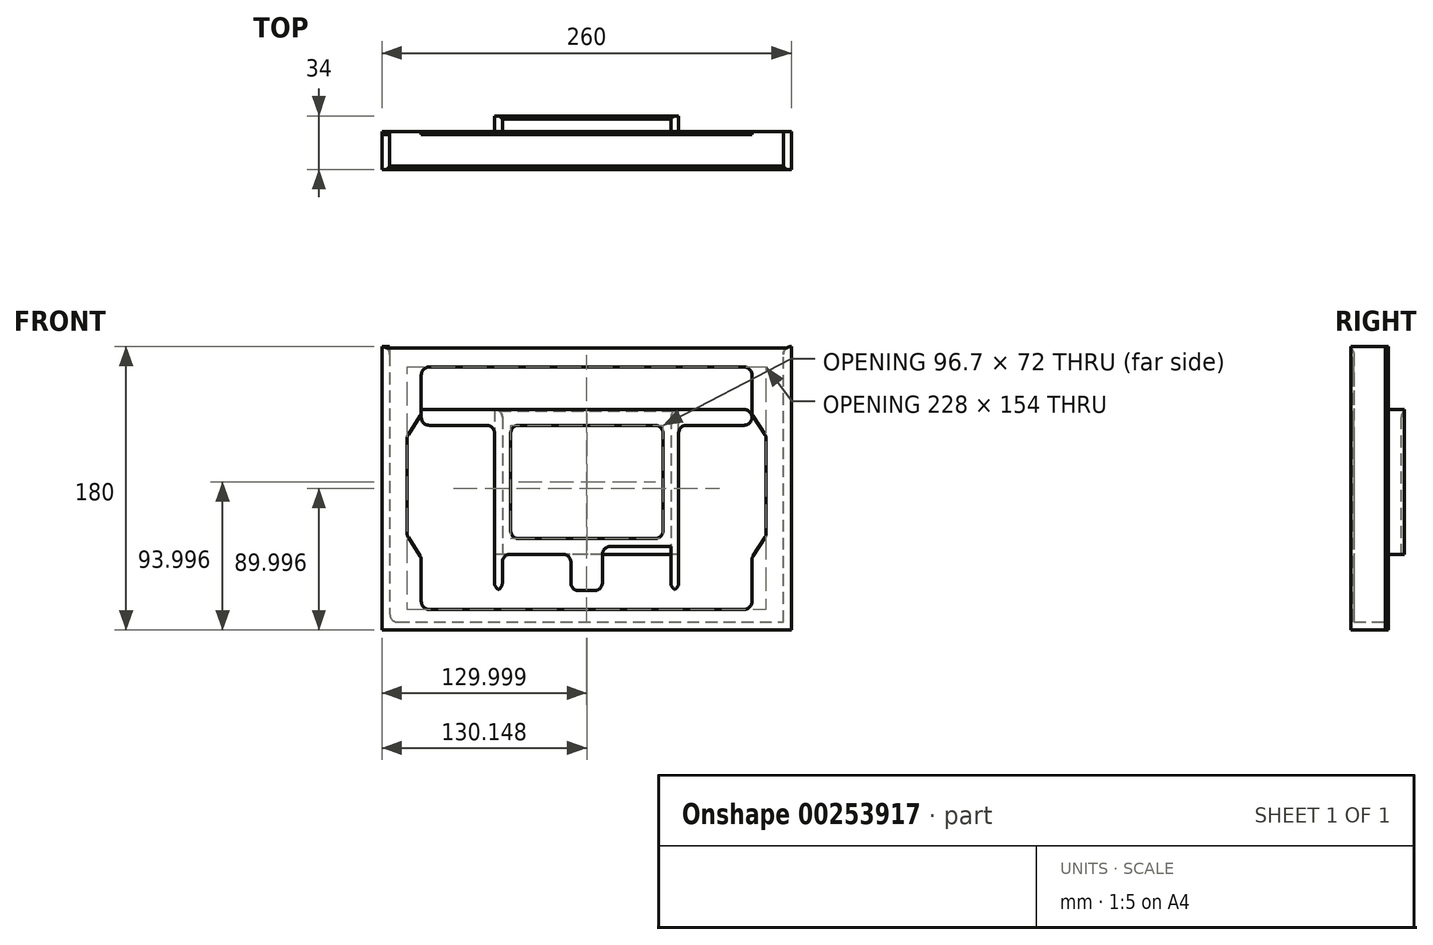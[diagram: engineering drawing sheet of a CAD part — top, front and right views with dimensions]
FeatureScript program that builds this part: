
annotation { "Feature Type Name" : "Feature", "Feature Type Description" : "" }
export const myFeature = defineFeature(function(context is Context, id is Id, definition is map)
    precondition{}
    {
        {
            var Q0;
            Q0=qCreatedBy(makeId("Front.planeOp"),FACE);
            var sketch = newSketch(context, id + "F0", { "sketchPlane" : qUnion([Q0])});
            skLineSegment(sketch, "E0", {"start": v(-163.92, 87.23) * mm, "end": v(-163.92, -87.77) * mm});
            skLineSegment(sketch, "E1", {"start": v(-163.92, -87.77) * mm, "end": v(86.08, -87.77) * mm});
            skLineSegment(sketch, "E2", {"start": v(86.08, -87.77) * mm, "end": v(86.08, 87.23) * mm});
            skLineSegment(sketch, "E3", {"start": v(86.08, 87.23) * mm, "end": v(91.08, 87.23) * mm});
            skLineSegment(sketch, "E4", {"start": v(91.08, 87.23) * mm, "end": v(91.08, -92.77) * mm});
            skLineSegment(sketch, "E5", {"start": v(91.08, -92.77) * mm, "end": v(-168.92, -92.77) * mm});
            skLineSegment(sketch, "E6", {"start": v(-168.92, -92.77) * mm, "end": v(-168.92, 87.23) * mm});
            skLineSegment(sketch, "E7", {"start": v(-168.92, 87.23) * mm, "end": v(-163.92, 87.23) * mm});
            skSolve(sketch);
        }
        {
            var Q0;
            Q0 = qSketchRegion(id + "F0", true);
            extrude(context, id + "F1", {"entities" : qUnion([Q0]), "depth" : 20 * mm});
        }
        {
            var Q0;
            Q0=makeQuery(id+"F1.opExtrude","CAP_FACE",FACE,{"disambiguationData":[OSD([sQuery(id+"F0.wireOp",EDGE,"E0"),sQuery(id+"F0.wireOp",EDGE,"E1"),sQuery(id+"F0.wireOp",EDGE,"E2"),sQuery(id+"F0.wireOp",EDGE,"E3"),sQuery(id+"F0.wireOp",EDGE,"E4"),sQuery(id+"F0.wireOp",EDGE,"E5"),sQuery(id+"F0.wireOp",EDGE,"E6"),sQuery(id+"F0.wireOp",EDGE,"E7")])],"isStart":false});
            var sketch = newSketch(context, id + "F2", { "sketchPlane" : qUnion([Q0])});
            skLineSegment(sketch, "E8", {"start": v(91.08, 87.23) * mm, "end": v(91.08, -92.77) * mm});
            skLineSegment(sketch, "E9", {"start": v(91.08, -92.77) * mm, "end": v(-168.92, -92.77) * mm});
            skLineSegment(sketch, "E10", {"start": v(-168.92, -92.77) * mm, "end": v(-168.92, 87.23) * mm});
            skLineSegment(sketch, "E11", {"start": v(-168.92, 87.23) * mm, "end": v(91.08, 87.23) * mm});
            skLineSegment(sketch, "E12", {"start": v(-143.92, 74.23) * mm, "end": v(-143.92, 44.23) * mm});
            skLineSegment(sketch, "E13", {"start": v(-152.92, 30.23) * mm, "end": v(-152.92, -32.96) * mm});
            skLineSegment(sketch, "E14", {"start": v(-143.92, -46.96) * mm, "end": v(-143.92, -79.77) * mm});
            skLineSegment(sketch, "E15", {"start": v(-143.92, 44.23) * mm, "end": v(-152.92, 30.23) * mm});
            skLineSegment(sketch, "E16", {"start": v(-143.92, -46.96) * mm, "end": v(-152.92, -32.96) * mm});
            skLineSegment(sketch, "E17", {"start": v(75.08, 30.23) * mm, "end": v(75.08, -32.96) * mm});
            skLineSegment(sketch, "E18", {"start": v(-143.92, 74.23) * mm, "end": v(66.08, 74.23) * mm});
            skLineSegment(sketch, "E19", {"start": v(66.08, -79.77) * mm, "end": v(-143.92, -79.77) * mm});
            skLineSegment(sketch, "E20", {"start": v(75.08, 30.23) * mm, "end": v(66.08, 44.23) * mm});
            skLineSegment(sketch, "E21", {"start": v(75.08, -32.96) * mm, "end": v(66.08, -46.96) * mm});
            skLineSegment(sketch, "E22", {"start": v(66.08, 44.23) * mm, "end": v(66.08, 74.23) * mm});
            skLineSegment(sketch, "E23", {"start": v(66.08, -46.96) * mm, "end": v(66.08, -79.77) * mm});
            skSolve(sketch);
        }
        {
            var Q0;
            Q0 = qSketchRegion(id + "F2", true);
            extrude(context, id + "F3", {"entities" : qUnion([Q0]), "operationType" : NewBodyOperationType.ADD, "depth" : 2 * mm});
        }
        {
            var Q0;
            Q0=makeQuery(id+"F0.imprint","IMPRINT",FACE,{"disambiguationData":[TD([[makeQuery(id+"F0.imprint","IMPRINT",EDGE,{"derivedFrom":sQuery(id+"F0.wireOp",EDGE,"E0")}),-1.0]])]});
            var sketch = newSketch(context, id + "F4", { "sketchPlane" : qUnion([Q0])});
            skLineSegment(sketch, "E24", {"start": v(91.08, 87.23) * mm, "end": v(91.08, -92.77) * mm});
            skLineSegment(sketch, "E25", {"start": v(91.08, -92.77) * mm, "end": v(-168.92, -92.77) * mm});
            skLineSegment(sketch, "E26", {"start": v(-168.92, -92.77) * mm, "end": v(-168.92, 87.23) * mm});
            skLineSegment(sketch, "E27", {"start": v(-168.92, 87.23) * mm, "end": v(-143.92, 87.23) * mm});
            skLineSegment(sketch, "E28", {"start": v(-143.92, 87.23) * mm, "end": v(-143.92, -87.77) * mm});
            skLineSegment(sketch, "E29", {"start": v(66.08, -87.77) * mm, "end": v(66.08, 87.23) * mm});
            skLineSegment(sketch, "E30", {"start": v(66.08, 87.23) * mm, "end": v(91.08, 87.23) * mm});
            skLineSegment(sketch, "E31", {"start": v(66.08, 87.23) * mm, "end": v(66.08, 47.23) * mm});
            skLineSegment(sketch, "E32", {"start": v(66.08, 47.23) * mm, "end": v(-143.92, 47.23) * mm});
            skLineSegment(sketch, "E33", {"start": v(-143.92, 47.23) * mm, "end": v(-143.92, 37.23) * mm});
            skLineSegment(sketch, "E34", {"start": v(-143.92, 37.23) * mm, "end": v(66.08, 37.23) * mm});
            skLineSegment(sketch, "E35", {"start": v(66.08, -87.77) * mm, "end": v(66.08, -67.77) * mm});
            skLineSegment(sketch, "E36", {"start": v(66.08, -67.77) * mm, "end": v(-143.92, -67.77) * mm});
            skLineSegment(sketch, "E37.bottom", {"start": v(66.08, 37.23) * mm, "end": v(14.58, 37.23) * mm});
            skLineSegment(sketch, "E37.top", {"start": v(66.08, 37.23) * mm, "end": v(14.58, 37.23) * mm});
            skLineSegment(sketch, "E37.left", {"start": v(66.08, 37.23) * mm, "end": v(66.08, 37.23) * mm});
            skLineSegment(sketch, "E37.right", {"start": v(14.58, 37.23) * mm, "end": v(14.58, 37.23) * mm});
            skLineSegment(sketch, "E38.bottom", {"start": v(-143.92, 37.23) * mm, "end": v(-92.42, 37.23) * mm});
            skLineSegment(sketch, "E38.top", {"start": v(-143.92, 37.23) * mm, "end": v(-92.42, 37.23) * mm});
            skLineSegment(sketch, "E38.left", {"start": v(-143.92, 37.23) * mm, "end": v(-143.92, 37.23) * mm});
            skLineSegment(sketch, "E38.right", {"start": v(-92.42, 37.23) * mm, "end": v(-92.42, 37.23) * mm});
            skLineSegment(sketch, "E39", {"start": v(14.58, 37.23) * mm, "end": v(14.58, -39.77) * mm});
            skLineSegment(sketch, "E40", {"start": v(14.58, -39.77) * mm, "end": v(-92.42, -39.77) * mm});
            skLineSegment(sketch, "E41", {"start": v(-92.42, -39.77) * mm, "end": v(-92.42, 37.23) * mm});
            skLineSegment(sketch, "E42", {"start": v(14.58, 37.23) * mm, "end": v(19.58, 37.23) * mm});
            skLineSegment(sketch, "E43", {"start": v(19.58, 37.23) * mm, "end": v(19.58, -58.16) * mm});
            skLineSegment(sketch, "E44", {"start": v(14.58, -39.77) * mm, "end": v(14.58, -67.77) * mm});
            skLineSegment(sketch, "E45", {"start": v(19.58, -58.16) * mm, "end": v(19.58, -67.77) * mm});
            skLineSegment(sketch, "E46", {"start": v(-92.42, 37.23) * mm, "end": v(-97.42, 37.23) * mm});
            skLineSegment(sketch, "E47", {"start": v(-97.42, 37.23) * mm, "end": v(-97.42, -67.77) * mm});
            skLineSegment(sketch, "E48", {"start": v(-92.42, -39.77) * mm, "end": v(-92.42, -67.77) * mm});
            skLineSegment(sketch, "E49", {"start": v(14.58, -67.77) * mm, "end": v(-28.92, -67.77) * mm});
            skLineSegment(sketch, "E50", {"start": v(-28.92, -67.77) * mm, "end": v(-28.92, -39.77) * mm});
            skLineSegment(sketch, "E51", {"start": v(-92.42, -67.77) * mm, "end": v(-48.92, -67.77) * mm});
            skLineSegment(sketch, "E52", {"start": v(-48.92, -67.77) * mm, "end": v(-48.92, -39.77) * mm});
            skLineSegment(sketch, "E53", {"start": v(14.58, -39.77) * mm, "end": v(14.58, -44.77) * mm});
            skLineSegment(sketch, "E54", {"start": v(14.58, -44.77) * mm, "end": v(-92.42, -44.77) * mm});
            skLineSegment(sketch, "E55", {"start": v(91.08, 87.23) * mm, "end": v(86.08, 87.23) * mm});
            skLineSegment(sketch, "E56", {"start": v(86.08, 87.23) * mm, "end": v(86.08, 47.23) * mm});
            skLineSegment(sketch, "E57", {"start": v(86.08, 47.23) * mm, "end": v(66.08, 47.23) * mm});
            skLineSegment(sketch, "E58", {"start": v(-168.92, 87.23) * mm, "end": v(-163.92, 87.23) * mm});
            skLineSegment(sketch, "E59", {"start": v(-163.92, 87.23) * mm, "end": v(-163.92, 47.23) * mm});
            skLineSegment(sketch, "E60", {"start": v(-163.92, 47.23) * mm, "end": v(-143.92, 47.23) * mm});
            skLineSegment(sketch, "E61", {"start": v(-92.42, 37.23) * mm, "end": v(-87.12, 37.23) * mm});
            skLineSegment(sketch, "E62", {"start": v(-87.12, 37.23) * mm, "end": v(-87.12, -34.77) * mm});
            skLineSegment(sketch, "E63", {"start": v(14.58, 37.23) * mm, "end": v(9.58, 37.23) * mm});
            skLineSegment(sketch, "E64", {"start": v(9.58, 37.23) * mm, "end": v(9.58, -34.77) * mm});
            skLineSegment(sketch, "E65", {"start": v(9.58, -34.77) * mm, "end": v(-87.12, -34.77) * mm});
            skSolve(sketch);
        }
        {
            var Q0;
            {var subQ0=sQuery(id+"F4.wireOp",EDGE,"E32");Q0=makeQuery(id+"F4.imprint","IMPRINT",FACE,{"disambiguationData":[TD([[makeQuery(id+"F4.imprint","IMPRINT",EDGE,{"derivedFrom":subQ0}),1.0]])]});}
            var Q1;
            Q1=makeQuery(id+"F4.imprint","IMPRINT",FACE,{"disambiguationData":[TD([[makeQuery(id+"F4.imprint","IMPRINT",EDGE,{"derivedFrom":makeQuery(id+"F0.imprint","IMPRINT",EDGE,{"derivedFrom":sQuery(id+"F0.wireOp",EDGE,"E0")})}),-1.0]])]});
            var Q2;
            {var subQ13=sQuery(id+"F4.wireOp",EDGE,"E26");Q2=makeQuery(id+"F4.imprint","IMPRINT",FACE,{"disambiguationData":[TD([[makeQuery(id+"F4.imprint","IMPRINT",EDGE,{"derivedFrom":subQ13}),-1.0]])]});}
            var Q3;
            Q3=makeQuery(id+"F4.imprint","IMPRINT",FACE,{"disambiguationData":[TD([[makeQuery(id+"F4.imprint","IMPRINT",EDGE,{"derivedFrom":sQuery(id+"F4.wireOp",EDGE,"E39")}),1.0]])]});
            var Q4;
            {var subQ0=sQuery(id+"F4.wireOp",EDGE,"E53");Q4=makeQuery(id+"F4.imprint","IMPRINT",FACE,{"disambiguationData":[TD([[makeQuery(id+"F4.imprint","IMPRINT",EDGE,{"derivedFrom":subQ0}),-1.0]])]});}
            var Q5;
            {var subQ0=sQuery(id+"F4.wireOp",EDGE,"E50");var subQ5=sQuery(id+"F4.wireOp",EDGE,"E54");var subQ6=makeQuery(id+"F4.imprint","INTERSECT",VERTEX,{"derivedFrom":[subQ0,subQ5]});Q5=makeQuery(id+"F4.imprint","IMPRINT",FACE,{"disambiguationData":[TD([[makeQuery(id+"F4.imprint","IMPRINT",EDGE,{"disambiguationData":[TD([[subQ6,-1.0]])],"derivedFrom":subQ5}),1.0]])]});}
            var Q6;
            {var subQ0=sQuery(id+"F4.wireOp",EDGE,"E50");var subQ1=sQuery(id+"F4.wireOp",EDGE,"E40");var subQ2=makeQuery(id+"F4.imprint","INTERSECT",VERTEX,{"derivedFrom":[subQ1,subQ0]});Q6=makeQuery(id+"F4.imprint","IMPRINT",FACE,{"disambiguationData":[TD([[makeQuery(id+"F4.imprint","IMPRINT",EDGE,{"disambiguationData":[TD([[subQ2,-1.0]])],"derivedFrom":subQ1}),1.0]])]});}
            var Q7;
            {var subQ1=sQuery(id+"F4.wireOp",EDGE,"E40");var subQ3=sQuery(id+"F4.wireOp",EDGE,"E52");var subQ4=makeQuery(id+"F4.imprint","INTERSECT",VERTEX,{"derivedFrom":[subQ1,subQ3]});Q7=makeQuery(id+"F4.imprint","IMPRINT",FACE,{"disambiguationData":[TD([[makeQuery(id+"F4.imprint","IMPRINT",EDGE,{"disambiguationData":[TD([[subQ4,1.0]])],"derivedFrom":subQ3}),1.0]])]});}
            var Q8;
            {var subQ5=sQuery(id+"F4.wireOp",EDGE,"E41");Q8=makeQuery(id+"F4.imprint","IMPRINT",FACE,{"disambiguationData":[TD([[makeQuery(id+"F4.imprint","IMPRINT",EDGE,{"derivedFrom":subQ5}),1.0]])]});}
            var Q9;
            {var subQ14=makeQuery(id+"F0.imprint","IMPRINT",EDGE,{"derivedFrom":sQuery(id+"F0.wireOp",EDGE,"E1")});Q9=makeQuery(id+"F4.imprint","IMPRINT",FACE,{"disambiguationData":[TD([[makeQuery(id+"F4.imprint","IMPRINT",EDGE,{"derivedFrom":subQ14}),-1.0]])]});}
            var Q10;
            {var subQ7=sQuery(id+"F4.wireOp",EDGE,"E33");Q10=makeQuery(id+"F4.imprint","IMPRINT",FACE,{"disambiguationData":[TD([[makeQuery(id+"F4.imprint","IMPRINT",EDGE,{"derivedFrom":subQ7}),-1.0]])]});}
            var Q11;
            {var subQ4=sQuery(id+"F4.wireOp",EDGE,"E39");Q11=makeQuery(id+"F4.imprint","IMPRINT",FACE,{"disambiguationData":[TD([[makeQuery(id+"F4.imprint","IMPRINT",EDGE,{"derivedFrom":subQ4}),-1.0]])]});}
            extrude(context, id + "F5", {"entities" : qUnion([Q0, Q1, Q2, Q3, Q4, Q5, Q6, Q7, Q8, Q9, Q10, Q11]), "operationType" : NewBodyOperationType.ADD, "oppositeDirection" : true, "depth" : 2 * mm});
        }
        {
            var Q0;
            Q0=makeQuery(id+"F5.opExtrude","CAP_FACE",FACE,{"disambiguationData":[OSD([sQuery(id+"F0.wireOp",EDGE,"E0"),sQuery(id+"F0.wireOp",EDGE,"E7"),sQuery(id+"F4.wireOp",EDGE,"E24"),sQuery(id+"F4.wireOp",EDGE,"E25"),sQuery(id+"F4.wireOp",EDGE,"E26"),sQuery(id+"F4.wireOp",EDGE,"E28"),sQuery(id+"F4.wireOp",EDGE,"E29"),sQuery(id+"F4.wireOp",EDGE,"E32"),sQuery(id+"F4.wireOp",EDGE,"E34"),sQuery(id+"F4.wireOp",EDGE,"E36"),sQuery(id+"F4.wireOp",EDGE,"E37.top"),sQuery(id+"F4.wireOp",EDGE,"E38.top"),sQuery(id+"F4.wireOp",EDGE,"E39"),sQuery(id+"F4.wireOp",EDGE,"E40"),sQuery(id+"F4.wireOp",EDGE,"E41"),sQuery(id+"F4.wireOp",EDGE,"E43"),sQuery(id+"F4.wireOp",EDGE,"E44"),sQuery(id+"F4.wireOp",EDGE,"E45"),sQuery(id+"F4.wireOp",EDGE,"E47"),sQuery(id+"F4.wireOp",EDGE,"E48"),sQuery(id+"F4.wireOp",EDGE,"E49"),sQuery(id+"F4.wireOp",EDGE,"E50"),sQuery(id+"F4.wireOp",EDGE,"E51"),sQuery(id+"F4.wireOp",EDGE,"E52"),sQuery(id+"F4.wireOp",EDGE,"E54"),sQuery(id+"F4.wireOp",EDGE,"E55"),sQuery(id+"F4.wireOp",EDGE,"E56"),sQuery(id+"F4.wireOp",EDGE,"E57"),sQuery(id+"F4.wireOp",EDGE,"E58"),sQuery(id+"F4.wireOp",EDGE,"E59"),sQuery(id+"F4.wireOp",EDGE,"E60")])],"isStart":false});
            var sketch = newSketch(context, id + "F6", { "sketchPlane" : qUnion([Q0])});
            skLineSegment(sketch, "E66", {"start": v(-19.58, 37.23) * mm, "end": v(-19.58, 47.23) * mm});
            skLineSegment(sketch, "E67", {"start": v(-19.58, 47.23) * mm, "end": v(-14.58, 47.23) * mm});
            skLineSegment(sketch, "E68", {"start": v(-19.58, 37.23) * mm, "end": v(-19.58, -44.77) * mm});
            skLineSegment(sketch, "E69", {"start": v(-19.58, -44.77) * mm, "end": v(97.42, -44.77) * mm});
            skLineSegment(sketch, "E70", {"start": v(97.42, -44.77) * mm, "end": v(97.42, 47.23) * mm});
            skLineSegment(sketch, "E71", {"start": v(97.42, 47.23) * mm, "end": v(92.42, 47.23) * mm});
            skLineSegment(sketch, "E72", {"start": v(92.42, 47.23) * mm, "end": v(92.42, -44.77) * mm});
            skLineSegment(sketch, "E73", {"start": v(92.42, -44.77) * mm, "end": v(-14.58, -44.77) * mm});
            skLineSegment(sketch, "E74", {"start": v(-14.58, -44.77) * mm, "end": v(-14.58, 47.23) * mm});
            skLineSegment(sketch, "E75", {"start": v(-14.58, -44.77) * mm, "end": v(-14.58, -39.77) * mm});
            skLineSegment(sketch, "E76", {"start": v(-14.58, -39.77) * mm, "end": v(92.42, -39.77) * mm});
            skLineSegment(sketch, "E77", {"start": v(92.42, -39.77) * mm, "end": v(92.42, -44.77) * mm});
            skSolve(sketch);
        }
        {
            var Q0;
            Q0=makeQuery(id+"F6.imprint","IMPRINT",FACE,{"disambiguationData":[TD([[makeQuery(id+"F6.imprint","IMPRINT",EDGE,{"derivedFrom":sQuery(id+"F6.wireOp",EDGE,"E66")}),-1.0]])]});
            var Q1;
            {var subQ0=sQuery(id+"F6.wireOp",EDGE,"E71");Q1=makeQuery(id+"F6.imprint","IMPRINT",FACE,{"disambiguationData":[TD([[makeQuery(id+"F6.imprint","IMPRINT",EDGE,{"derivedFrom":subQ0}),-1.0]])]});}
            var Q2;
            {var subQ5=sQuery(id+"F6.wireOp",EDGE,"E75");Q2=makeQuery(id+"F6.imprint","IMPRINT",FACE,{"disambiguationData":[TD([[makeQuery(id+"F6.imprint","IMPRINT",EDGE,{"derivedFrom":subQ5}),-1.0]])]});}
            extrude(context, id + "F7", {"entities" : qUnion([Q0, Q1, Q2]), "operationType" : NewBodyOperationType.ADD, "depth" : 8 * mm});
        }
        {
            var Q0;
            Q0=makeQuery(id+"F7.opExtrude","CAP_FACE",FACE,{"disambiguationData":[OSD([sQuery(id+"F6.wireOp",EDGE,"E66"),sQuery(id+"F6.wireOp",EDGE,"E67"),sQuery(id+"F6.wireOp",EDGE,"E68"),sQuery(id+"F6.wireOp",EDGE,"E69"),sQuery(id+"F6.wireOp",EDGE,"E70"),sQuery(id+"F6.wireOp",EDGE,"E71"),sQuery(id+"F6.wireOp",EDGE,"E72"),sQuery(id+"F6.wireOp",EDGE,"E73"),sQuery(id+"F6.wireOp",EDGE,"E74")])],"isStart":false});
            var sketch = newSketch(context, id + "F8", { "sketchPlane" : qUnion([Q0])});
            skLineSegment(sketch, "E78.bottom", {"start": v(-19.58, 47.23) * mm, "end": v(97.42, 47.23) * mm});
            skLineSegment(sketch, "E78.top", {"start": v(-19.58, -44.77) * mm, "end": v(97.42, -44.77) * mm});
            skLineSegment(sketch, "E78.left", {"start": v(-19.58, 47.23) * mm, "end": v(-19.58, -44.77) * mm});
            skLineSegment(sketch, "E78.right", {"start": v(97.42, 47.23) * mm, "end": v(97.42, -44.77) * mm});
            skSolve(sketch);
        }
        {
            var Q0;
            Q0 = qSketchRegion(id + "F8", true);
            extrude(context, id + "F9", {"entities" : qUnion([Q0]), "operationType" : NewBodyOperationType.ADD, "depth" : 2 * mm});
        }
        {
            var Q0;
            {var subQ0=sQuery(id+"F0.wireOp",EDGE,"E7");var subQ1=sQuery(id+"F0.wireOp",EDGE,"E0");Q0=makeQuery(id+"F5.boolean.opBoolean","MERGE",EDGE,{"derivedFrom":[makeQuery(id+"F1.opExtrude","SWEPT_EDGE",EDGE,{"disambiguationData":[OSD([subQ1,subQ0])]}),makeQuery(id+"F5.opExtrude","SWEPT_EDGE",EDGE,{"disambiguationData":[OSD([subQ1,subQ0])]})]});}
            var Q1;
            Q1=makeQuery(id+"F1.opExtrude","SWEPT_EDGE",EDGE,{"disambiguationData":[OSD([sQuery(id+"F0.wireOp",EDGE,"E2"),sQuery(id+"F0.wireOp",EDGE,"E3")])]});
            var Q2;
            Q2=makeQuery(id+"F7.opExtrude","SWEPT_EDGE",EDGE,{"disambiguationData":[OSD([sQuery(id+"F4.wireOp",EDGE,"E32"),sQuery(id+"F4.wireOp",EDGE,"E57"),sQuery(id+"F4.wireOp",EDGE,"E60"),sQuery(id+"F6.wireOp",EDGE,"E67"),sQuery(id+"F6.wireOp",EDGE,"E74")])]});
            var Q3;
            Q3=makeQuery(id+"F7.opExtrude","SWEPT_EDGE",EDGE,{"disambiguationData":[OSD([sQuery(id+"F4.wireOp",EDGE,"E32"),sQuery(id+"F4.wireOp",EDGE,"E57"),sQuery(id+"F4.wireOp",EDGE,"E60"),sQuery(id+"F6.wireOp",EDGE,"E71"),sQuery(id+"F6.wireOp",EDGE,"E72")])]});
            var Q4;
            Q4=makeQuery(id+"F9.opExtrude","CAP_EDGE",EDGE,{"disambiguationData":[OSD([sQuery(id+"F8.wireOp",EDGE,"E78.bottom")])],"isStart":true});
            var Q5;
            Q5=makeQuery(id+"F5.opExtrude","SWEPT_EDGE",EDGE,{"disambiguationData":[OSD([sQuery(id+"F4.wireOp",EDGE,"E34"),sQuery(id+"F4.wireOp",EDGE,"E63"),sQuery(id+"F4.wireOp",EDGE,"E64")])]});
            var Q6;
            Q6=makeQuery(id+"F5.opExtrude","SWEPT_EDGE",EDGE,{"disambiguationData":[OSD([sQuery(id+"F4.wireOp",EDGE,"E34"),sQuery(id+"F4.wireOp",EDGE,"E61"),sQuery(id+"F4.wireOp",EDGE,"E62")])]});
            var Q7;
            Q7=makeQuery(id+"F5.opExtrude","SWEPT_EDGE",EDGE,{"disambiguationData":[OSD([sQuery(id+"F4.wireOp",EDGE,"E62"),sQuery(id+"F4.wireOp",EDGE,"E65")])]});
            var Q8;
            Q8=makeQuery(id+"F5.opExtrude","SWEPT_EDGE",EDGE,{"disambiguationData":[OSD([sQuery(id+"F4.wireOp",EDGE,"E64"),sQuery(id+"F4.wireOp",EDGE,"E65")])]});
            var Q9;
            Q9=makeQuery(id+"F5.opExtrude","SWEPT_EDGE",EDGE,{"disambiguationData":[OSD([sQuery(id+"F4.wireOp",EDGE,"E36"),sQuery(id+"F4.wireOp",EDGE,"E44"),sQuery(id+"F4.wireOp",EDGE,"E49")])]});
            var Q10;
            Q10=makeQuery(id+"F5.opExtrude","SWEPT_EDGE",EDGE,{"disambiguationData":[OSD([sQuery(id+"F4.wireOp",EDGE,"E44"),sQuery(id+"F4.wireOp",EDGE,"E53"),sQuery(id+"F4.wireOp",EDGE,"E54")])]});
            var Q11;
            Q11=makeQuery(id+"F5.opExtrude","SWEPT_EDGE",EDGE,{"disambiguationData":[OSD([sQuery(id+"F4.wireOp",EDGE,"E36"),sQuery(id+"F4.wireOp",EDGE,"E49"),sQuery(id+"F4.wireOp",EDGE,"E50")])]});
            var Q12;
            Q12=makeQuery(id+"F5.opExtrude","SWEPT_EDGE",EDGE,{"disambiguationData":[OSD([sQuery(id+"F4.wireOp",EDGE,"E50"),sQuery(id+"F4.wireOp",EDGE,"E54")])]});
            var Q13;
            Q13=makeQuery(id+"F5.opExtrude","SWEPT_EDGE",EDGE,{"disambiguationData":[OSD([sQuery(id+"F4.wireOp",EDGE,"E29"),sQuery(id+"F4.wireOp",EDGE,"E36")])]});
            var Q14;
            Q14=makeQuery(id+"F5.opExtrude","SWEPT_EDGE",EDGE,{"disambiguationData":[OSD([sQuery(id+"F4.wireOp",EDGE,"E36"),sQuery(id+"F4.wireOp",EDGE,"E45")])]});
            var Q15;
            Q15=makeQuery(id+"F5.opExtrude","SWEPT_EDGE",EDGE,{"disambiguationData":[OSD([sQuery(id+"F4.wireOp",EDGE,"E36"),sQuery(id+"F4.wireOp",EDGE,"E48"),sQuery(id+"F4.wireOp",EDGE,"E51")])]});
            var Q16;
            Q16=makeQuery(id+"F5.opExtrude","SWEPT_EDGE",EDGE,{"disambiguationData":[OSD([sQuery(id+"F4.wireOp",EDGE,"E36"),sQuery(id+"F4.wireOp",EDGE,"E51"),sQuery(id+"F4.wireOp",EDGE,"E52")])]});
            var Q17;
            Q17=makeQuery(id+"F5.opExtrude","SWEPT_EDGE",EDGE,{"disambiguationData":[OSD([sQuery(id+"F4.wireOp",EDGE,"E48"),sQuery(id+"F4.wireOp",EDGE,"E54")])]});
            var Q18;
            Q18=makeQuery(id+"F5.opExtrude","SWEPT_EDGE",EDGE,{"disambiguationData":[OSD([sQuery(id+"F4.wireOp",EDGE,"E52"),sQuery(id+"F4.wireOp",EDGE,"E54")])]});
            var Q19;
            Q19=makeQuery(id+"F5.opExtrude","SWEPT_EDGE",EDGE,{"disambiguationData":[OSD([sQuery(id+"F4.wireOp",EDGE,"E36"),sQuery(id+"F4.wireOp",EDGE,"E47")])]});
            var Q20;
            Q20=makeQuery(id+"F5.opExtrude","SWEPT_EDGE",EDGE,{"disambiguationData":[OSD([sQuery(id+"F4.wireOp",EDGE,"E28"),sQuery(id+"F4.wireOp",EDGE,"E36")])]});
            var Q21;
            Q21=makeQuery(id+"F5.opExtrude","SWEPT_EDGE",EDGE,{"disambiguationData":[OSD([sQuery(id+"F4.wireOp",EDGE,"E28"),sQuery(id+"F4.wireOp",EDGE,"E33"),sQuery(id+"F4.wireOp",EDGE,"E38.top")])]});
            var Q22;
            Q22=makeQuery(id+"F5.opExtrude","SWEPT_EDGE",EDGE,{"disambiguationData":[OSD([sQuery(id+"F4.wireOp",EDGE,"E38.top"),sQuery(id+"F4.wireOp",EDGE,"E46"),sQuery(id+"F4.wireOp",EDGE,"E47")])]});
            var Q23;
            Q23=makeQuery(id+"F3.opExtrude","SWEPT_EDGE",EDGE,{"disambiguationData":[OSD([sQuery(id+"F2.wireOp",EDGE,"E12"),sQuery(id+"F2.wireOp",EDGE,"E18")])]});
            var Q24;
            Q24=makeQuery(id+"F3.opExtrude","SWEPT_EDGE",EDGE,{"disambiguationData":[OSD([sQuery(id+"F2.wireOp",EDGE,"E18"),sQuery(id+"F2.wireOp",EDGE,"E22")])]});
            var Q25;
            Q25=makeQuery(id+"F3.opExtrude","SWEPT_EDGE",EDGE,{"disambiguationData":[OSD([sQuery(id+"F2.wireOp",EDGE,"E20"),sQuery(id+"F2.wireOp",EDGE,"E22")])]});
            var Q26;
            Q26=makeQuery(id+"F3.opExtrude","SWEPT_EDGE",EDGE,{"disambiguationData":[OSD([sQuery(id+"F2.wireOp",EDGE,"E17"),sQuery(id+"F2.wireOp",EDGE,"E20")])]});
            var Q27;
            Q27=makeQuery(id+"F3.opExtrude","SWEPT_EDGE",EDGE,{"disambiguationData":[OSD([sQuery(id+"F2.wireOp",EDGE,"E17"),sQuery(id+"F2.wireOp",EDGE,"E21")])]});
            var Q28;
            Q28=makeQuery(id+"F3.opExtrude","SWEPT_EDGE",EDGE,{"disambiguationData":[OSD([sQuery(id+"F2.wireOp",EDGE,"E21"),sQuery(id+"F2.wireOp",EDGE,"E23")])]});
            var Q29;
            Q29=makeQuery(id+"F3.opExtrude","SWEPT_EDGE",EDGE,{"disambiguationData":[OSD([sQuery(id+"F2.wireOp",EDGE,"E19"),sQuery(id+"F2.wireOp",EDGE,"E23")])]});
            var Q30;
            Q30=makeQuery(id+"F3.opExtrude","SWEPT_EDGE",EDGE,{"disambiguationData":[OSD([sQuery(id+"F2.wireOp",EDGE,"E14"),sQuery(id+"F2.wireOp",EDGE,"E19")])]});
            var Q31;
            Q31=makeQuery(id+"F3.opExtrude","SWEPT_EDGE",EDGE,{"disambiguationData":[OSD([sQuery(id+"F2.wireOp",EDGE,"E14"),sQuery(id+"F2.wireOp",EDGE,"E16")])]});
            var Q32;
            Q32=makeQuery(id+"F3.opExtrude","SWEPT_EDGE",EDGE,{"disambiguationData":[OSD([sQuery(id+"F2.wireOp",EDGE,"E13"),sQuery(id+"F2.wireOp",EDGE,"E16")])]});
            var Q33;
            Q33=makeQuery(id+"F3.opExtrude","SWEPT_EDGE",EDGE,{"disambiguationData":[OSD([sQuery(id+"F2.wireOp",EDGE,"E13"),sQuery(id+"F2.wireOp",EDGE,"E15")])]});
            var Q34;
            Q34=makeQuery(id+"F3.opExtrude","SWEPT_EDGE",EDGE,{"disambiguationData":[OSD([sQuery(id+"F2.wireOp",EDGE,"E12"),sQuery(id+"F2.wireOp",EDGE,"E15")])]});
            var Q35;
            Q35=makeQuery(id+"F5.opExtrude","SWEPT_EDGE",EDGE,{"disambiguationData":[OSD([sQuery(id+"F4.wireOp",EDGE,"E56"),sQuery(id+"F4.wireOp",EDGE,"E57")])]});
            var Q36;
            Q36=makeQuery(id+"F5.opExtrude","SWEPT_EDGE",EDGE,{"disambiguationData":[OSD([sQuery(id+"F0.wireOp",EDGE,"E0"),sQuery(id+"F4.wireOp",EDGE,"E60")])]});
            var Q37;
            Q37=makeQuery(id+"F3.opExtrude","CAP_EDGE",EDGE,{"disambiguationData":[OSD([sQuery(id+"F2.wireOp",EDGE,"E11")])],"isStart":true});
            var Q38;
            Q38=makeQuery(id+"F5.opExtrude","SWEPT_EDGE",EDGE,{"disambiguationData":[OSD([sQuery(id+"F4.wireOp",EDGE,"E29"),sQuery(id+"F4.wireOp",EDGE,"E37.top")])]});
            var Q39;
            Q39=makeQuery(id+"F5.opExtrude","SWEPT_EDGE",EDGE,{"disambiguationData":[OSD([sQuery(id+"F4.wireOp",EDGE,"E37.top"),sQuery(id+"F4.wireOp",EDGE,"E42"),sQuery(id+"F4.wireOp",EDGE,"E43")])]});
            fillet(context, id + "F10", {"entities" : qUnion([Q0, Q1, Q2, Q3, Q4, Q5, Q6, Q7, Q8, Q9, Q10, Q11, Q12, Q13, Q14, Q15, Q16, Q17, Q18, Q19, Q20, Q21, Q22, Q23, Q24, Q25, Q26, Q27, Q28, Q29, Q30, Q31, Q32, Q33, Q34, Q35, Q36, Q37, Q38, Q39]), "radius" : 5 * mm, "tangentPropagation" : true, "allowEdgeOverflow" : false});
        }
    });
